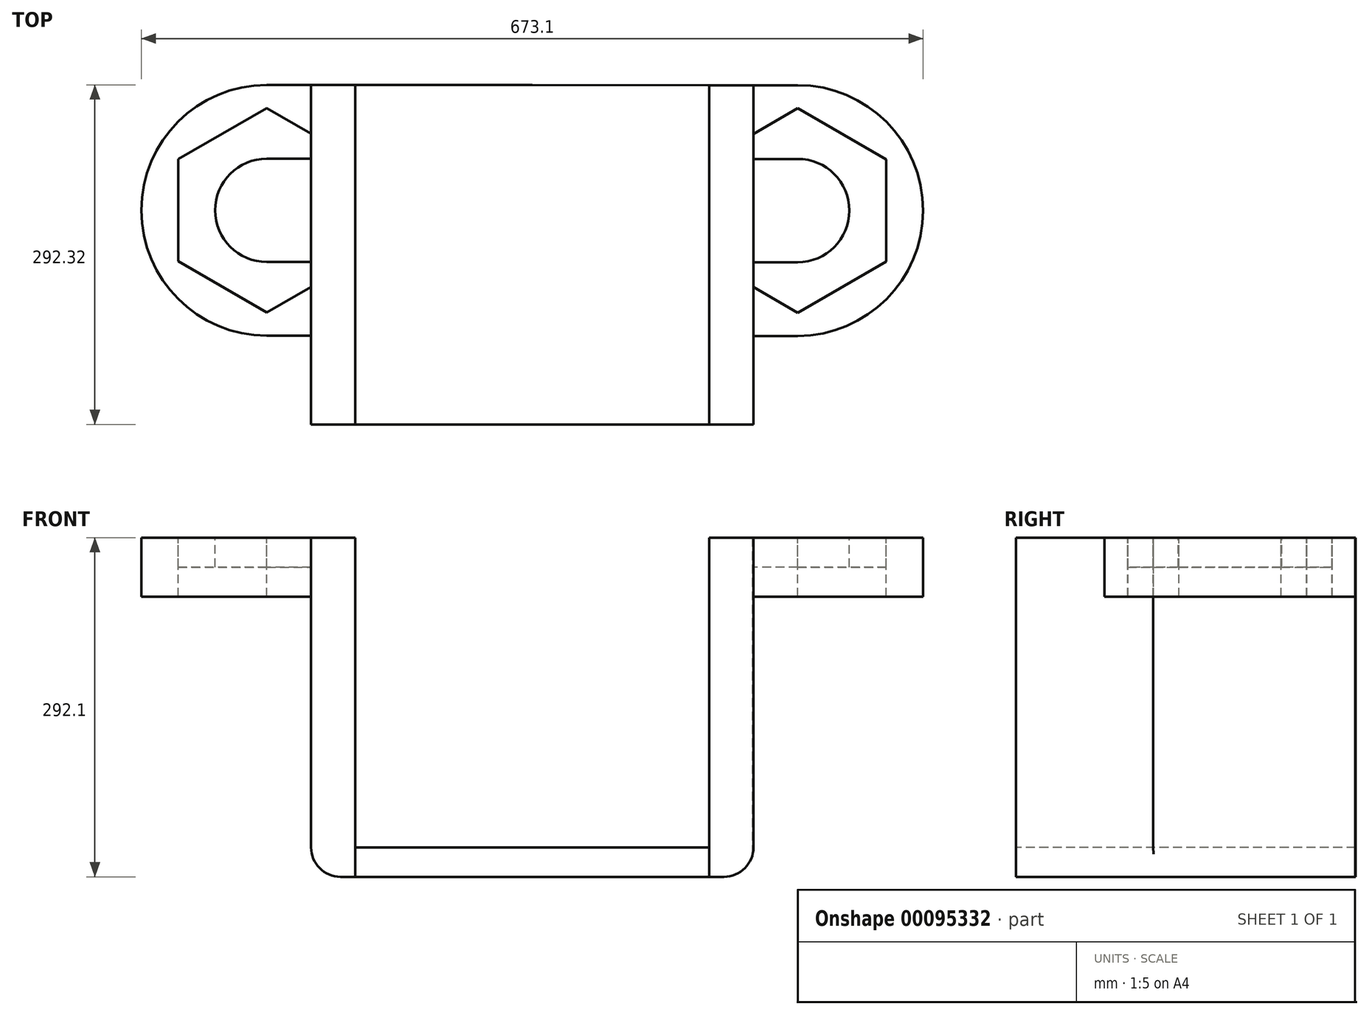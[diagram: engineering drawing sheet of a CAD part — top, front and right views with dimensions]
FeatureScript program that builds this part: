
annotation { "Feature Type Name" : "Feature", "Feature Type Description" : "" }
export const myFeature = defineFeature(function(context is Context, id is Id, definition is map)
    precondition{}
    {
        {
            var Q0;
            Q0=qCreatedBy(makeId("Top.planeOp"),FACE);
            var sketch = newSketch(context, id + "F0", { "sketchPlane" : qUnion([Q0])});
            skLineSegment(sketch, "E0.bottom", {"start": v(-146.94, 152.89) * mm, "end": v(157.86, 152.67) * mm});
            skLineSegment(sketch, "E0.left", {"start": v(-146.94, 152.89) * mm, "end": v(-146.94, 152.87) * mm});
            skPoint(sketch, "E0.middle", {"position": v(0, 0) * mm});
            skLineSegment(sketch, "E1.bottom", {"start": v(157.86, 152.67) * mm, "end": v(195.96, 152.67) * mm});
            skLineSegment(sketch, "E1.top", {"start": v(157.86, -139.43) * mm, "end": v(195.96, -139.43) * mm});
            skLineSegment(sketch, "E1.left", {"start": v(157.86, 152.67) * mm, "end": v(157.86, 45.47) * mm});
            skLineSegment(sketch, "E1.right", {"start": v(195.96, 152.67) * mm, "end": v(195.96, -139.43) * mm});
            skLineSegment(sketch, "E2.bottom", {"start": v(-146.94, 152.89) * mm, "end": v(-185.04, 152.89) * mm});
            skLineSegment(sketch, "E2.top", {"start": v(-146.94, -139.43) * mm, "end": v(-185.04, -139.43) * mm});
            skLineSegment(sketch, "E2.left", {"start": v(-146.94, 152.89) * mm, "end": v(-146.94, -139.43) * mm});
            skLineSegment(sketch, "E2.right", {"start": v(-185.04, 152.89) * mm, "end": v(-185.04, -139.43) * mm});
            skLineSegment(sketch, "E3", {"start": v(-185.04, 152.89) * mm, "end": v(-223.14, 152.89) * mm});
            skLineSegment(sketch, "E4", {"start": v(195.96, 152.67) * mm, "end": v(234.06, 152.67) * mm});
            skLineSegment(sketch, "E5", {"start": v(195.96, -63.23) * mm, "end": v(234.06, -63.23) * mm});
            skLineSegment(sketch, "E6", {"start": v(-223.14, -63.01) * mm, "end": v(-185.04, -63.01) * mm});
            skArc(sketch, "E7", {"start": v(234.06, 152.67) * mm, "mid": v(342.01, 44.72) * mm, "end": v(234.06, -63.23) * mm});
            skArc(sketch, "E8", {"start": v(-223.14, 152.89) * mm, "mid": v(-331.09, 44.94) * mm, "end": v(-223.14, -63.01) * mm});
            skLineSegment(sketch, "E9", {"start": v(-185.04, 152.89) * mm, "end": v(195.96, 152.67) * mm});
            skLineSegment(sketch, "E10", {"start": v(195.96, -139.43) * mm, "end": v(-185.04, -139.43) * mm});
            skLineSegment(sketch, "E11", {"start": v(-185.04, -139.43) * mm, "end": v(195.96, -139.43) * mm});
            skLineSegment(sketch, "E12", {"start": v(-232.75, -62.58) * mm, "end": v(-232.75, -63.01) * mm});
            skLineSegment(sketch, "E13", {"start": v(-185.04, 152.89) * mm, "end": v(-146.94, 152.89) * mm});
            skLineSegment(sketch, "E14", {"start": v(-185.04, -139.43) * mm, "end": v(-146.94, -139.43) * mm});
            skPoint(sketch, "E15.trimOffspring.end.orphan", {"position": v(-157.86, -152.67) * mm});
            skLineSegment(sketch, "E16.0", {"start": v(-146.93, 88.94) * mm, "end": v(-146.94, 0.94) * mm});
            skLineSegment(sketch, "E16.1", {"start": v(-185.06, -21.06) * mm, "end": v(-223.16, -43.04) * mm});
            skLineSegment(sketch, "E16.2", {"start": v(-223.16, -43.04) * mm, "end": v(-299.35, 0.96) * mm});
            skLineSegment(sketch, "E16.3", {"start": v(-299.35, 0.96) * mm, "end": v(-299.34, 88.95) * mm});
            skLineSegment(sketch, "E16.4", {"start": v(-299.34, 88.95) * mm, "end": v(-223.14, 132.92) * mm});
            skLineSegment(sketch, "E16.5", {"start": v(-223.14, 132.92) * mm, "end": v(-185.04, 110.93) * mm});
            skPoint(sketch, "E16.0.midPoint", {"position": v(-146.94, 44.94) * mm});
            skLineSegment(sketch, "E17.5", {"start": v(195.96, -21.28) * mm, "end": v(195.32, -20.9) * mm});
            skPoint(sketch, "E17.0.midPoint", {"position": v(157.86, 45.47) * mm});
            skLineSegment(sketch, "E18", {"start": v(195.96, 152.67) * mm, "end": v(195.96, -63.23) * mm});
            skLineSegment(sketch, "E19", {"start": v(-185.04, 152.89) * mm, "end": v(-185.04, -63.01) * mm});
            skLineSegment(sketch, "E20", {"start": v(-276.99, 138.5) * mm, "end": v(-276.99, 101.84) * mm});
            skLineSegment(sketch, "E21", {"start": v(-277, -11.95) * mm, "end": v(-277, -48.62) * mm});
            skPoint(sketch, "E22.trimOffspring.end.orphan", {"position": v(146.94, -152.89) * mm});
            skLineSegment(sketch, "E23", {"start": v(157.86, 152.67) * mm, "end": v(157.86, -139.43) * mm});
            skLineSegment(sketch, "E24.0", {"start": v(157.86, 0.73) * mm, "end": v(157.86, 88.71) * mm});
            skLineSegment(sketch, "E24.1", {"start": v(195.96, 110.71) * mm, "end": v(234.06, 132.7) * mm});
            skLineSegment(sketch, "E24.2", {"start": v(234.06, 132.7) * mm, "end": v(310.26, 88.71) * mm});
            skLineSegment(sketch, "E24.3", {"start": v(310.26, 88.71) * mm, "end": v(310.26, 0.73) * mm});
            skLineSegment(sketch, "E24.4", {"start": v(310.26, 0.73) * mm, "end": v(234.06, -43.27) * mm});
            skLineSegment(sketch, "E24.5", {"start": v(234.06, -43.27) * mm, "end": v(195.32, -20.9) * mm});
            skPoint(sketch, "E24.0.midPoint", {"position": v(157.86, 44.72) * mm});
            skLineSegment(sketch, "E25", {"start": v(288.01, 138.22) * mm, "end": v(288.01, 101.56) * mm});
            skLineSegment(sketch, "E26", {"start": v(288.01, -48.78) * mm, "end": v(288.01, -12.12) * mm});
            skLineSegment(sketch, "E27.trimOffspring", {"start": v(288.01, -12.12) * mm, "end": v(288.01, -48.78) * mm});
            skArc(sketch, "E28", {"start": v(-223.14, 89.39) * mm, "mid": v(-267.59, 44.94) * mm, "end": v(-223.14, 0.49) * mm});
            skArc(sketch, "E29", {"start": v(234.06, 89.17) * mm, "mid": v(278.51, 44.72) * mm, "end": v(234.06, 0.27) * mm});
            skLineSegment(sketch, "E30", {"start": v(234.06, 89.17) * mm, "end": v(195.96, 89.17) * mm});
            skLineSegment(sketch, "E31", {"start": v(234.06, 0.27) * mm, "end": v(195.96, 0.27) * mm});
            skLineSegment(sketch, "E32", {"start": v(-223.14, 0.49) * mm, "end": v(-185.04, 0.49) * mm});
            skLineSegment(sketch, "E33", {"start": v(-223.14, 89.39) * mm, "end": v(-185.04, 89.39) * mm});
            skLineSegment(sketch, "E34", {"start": v(-185.06, -21.06) * mm, "end": v(-185.04, -63.01) * mm});
            skLineSegment(sketch, "E35", {"start": v(-185.06, -21.06) * mm, "end": v(-185.04, 0.49) * mm});
            skLineSegment(sketch, "E36", {"start": v(-185.04, 0.49) * mm, "end": v(-223.14, 0.49) * mm});
            skSolve(sketch);
        }
        {
            var Q0;
            {var subQ4=sQuery(id+"F0.wireOp",EDGE,"E2.right");Q0=makeQuery(id+"F0.imprint","IMPRINT",FACE,{"disambiguationData":[TD([[makeQuery(id+"F0.imprint","IMPRINT",EDGE,{"derivedFrom":subQ4}),1.0]])]});}
            var Q1;
            {var subQ5=sQuery(id+"F0.wireOp",EDGE,"E1.right");Q1=makeQuery(id+"F0.imprint","IMPRINT",FACE,{"disambiguationData":[TD([[makeQuery(id+"F0.imprint","IMPRINT",EDGE,{"derivedFrom":subQ5}),-1.0]])]});}
            extrude(context, id + "F1", {"entities" : qUnion([Q0, Q1]), "oppositeDirection" : true, "depth" : 292.1 * mm});
        }
        {
            var Q0;
            {var subQ3=sQuery(id+"F0.wireOp",EDGE,"E2.left");var subQ7=makeQuery(id+"F0.imprint","IMPRINT",VERTEX,{"derivedFrom":subQ3});Q0=makeQuery(id+"F0.imprint","IMPRINT",FACE,{"disambiguationData":[TD([[makeQuery(id+"F0.imprint","IMPRINT",EDGE,{"disambiguationData":[TD([[subQ7,1.0]])],"derivedFrom":subQ3}),1.0]])]});}
            extrude(context, id + "F2", {"entities" : qUnion([Q0]), "oppositeDirection" : true, "depth" : 292.1 * mm});
        }
        {
            var Q0;
            {var subQ1=sQuery(id+"F0.wireOp",EDGE,"E16.3");Q0=makeQuery(id+"F0.imprint","IMPRINT",FACE,{"disambiguationData":[TD([[makeQuery(id+"F0.imprint","IMPRINT",EDGE,{"derivedFrom":subQ1}),1.0]])]});}
            var Q1;
            {var subQ3=sQuery(id+"F0.wireOp",EDGE,"E3");Q1=makeQuery(id+"F0.imprint","IMPRINT",FACE,{"disambiguationData":[TD([[makeQuery(id+"F0.imprint","IMPRINT",EDGE,{"derivedFrom":subQ3}),1.0]])]});}
            var Q2;
            {var subQ4=sQuery(id+"F0.wireOp",EDGE,"E6");Q2=makeQuery(id+"F0.imprint","IMPRINT",FACE,{"disambiguationData":[TD([[makeQuery(id+"F0.imprint","IMPRINT",EDGE,{"derivedFrom":subQ4}),1.0]])]});}
            var Q3;
            {var subQ8=sQuery(id+"F0.wireOp",EDGE,"E5");Q3=makeQuery(id+"F0.imprint","IMPRINT",FACE,{"disambiguationData":[TD([[makeQuery(id+"F0.imprint","IMPRINT",EDGE,{"derivedFrom":subQ8}),1.0]])]});}
            var Q4;
            {var subQ1=sQuery(id+"F0.wireOp",EDGE,"E24.3");Q4=makeQuery(id+"F0.imprint","IMPRINT",FACE,{"disambiguationData":[TD([[makeQuery(id+"F0.imprint","IMPRINT",EDGE,{"derivedFrom":subQ1}),1.0]])]});}
            var Q5;
            {var subQ2=sQuery(id+"F0.wireOp",EDGE,"E4");Q5=makeQuery(id+"F0.imprint","IMPRINT",FACE,{"disambiguationData":[TD([[makeQuery(id+"F0.imprint","IMPRINT",EDGE,{"derivedFrom":subQ2}),-1.0]])]});}
            extrude(context, id + "F3", {"entities" : qUnion([Q0, Q1, Q2, Q3, Q4, Q5]), "oppositeDirection" : true, "depth" : 50.8 * mm});
        }
        {
            var Q0;
            {var subQ8=sQuery(id+"F0.wireOp",EDGE,"E24.1");Q0=makeQuery(id+"F0.imprint","IMPRINT",FACE,{"disambiguationData":[TD([[makeQuery(id+"F0.imprint","IMPRINT",EDGE,{"derivedFrom":subQ8}),-1.0]])]});}
            var Q1;
            {var subQ5=sQuery(id+"F0.wireOp",EDGE,"E16.3");Q1=makeQuery(id+"F0.imprint","IMPRINT",FACE,{"disambiguationData":[TD([[makeQuery(id+"F0.imprint","IMPRINT",EDGE,{"derivedFrom":subQ5}),-1.0]])]});}
            extrude(context, id + "F4", {"entities" : qUnion([Q0, Q1]), "oppositeDirection" : true, "depth" : 25.4 * mm});
        }
        {
            var Q0;
            {var subQ3=sQuery(id+"F0.wireOp",EDGE,"E2.left");var subQ7=makeQuery(id+"F0.imprint","IMPRINT",VERTEX,{"derivedFrom":subQ3});Q0=makeQuery(id+"F0.imprint","IMPRINT",FACE,{"disambiguationData":[TD([[makeQuery(id+"F0.imprint","IMPRINT",EDGE,{"disambiguationData":[TD([[subQ7,1.0]])],"derivedFrom":subQ3}),1.0]])]});}
            extrude(context, id + "F5", {"entities" : qUnion([Q0]), "operationType" : NewBodyOperationType.REMOVE, "oppositeDirection" : true, "depth" : 266.7 * mm});
        }
        {
            var Q0;
            Q0=makeQuery(id+"F1.opExtrude","CAP_EDGE",EDGE,{"disambiguationData":[OSD([sQuery(id+"F0.wireOp",EDGE,"E2.right"),sQuery(id+"F0.wireOp",EDGE,"E19")])],"isStart":false});
            fillet(context, id + "F6", {"entities" : qUnion([Q0]), "radius" : 25.4 * mm, "tangentPropagation" : true, "allowEdgeOverflow" : false});
        }
        {
            var Q0;
            Q0=makeQuery(id+"F1.opExtrude","CAP_EDGE",EDGE,{"disambiguationData":[OSD([sQuery(id+"F0.wireOp",EDGE,"E1.right"),sQuery(id+"F0.wireOp",EDGE,"E18")])],"isStart":false});
            var Q1;
            Q1=makeQuery(id+"F1.opExtrude","CAP_EDGE",EDGE,{"disambiguationData":[OSD([sQuery(id+"F0.wireOp",EDGE,"E18")])],"isStart":false});
            fillet(context, id + "F7", {"entities" : qUnion([Q0, Q1]), "radius" : 25.4 * mm, "tangentPropagation" : true, "allowEdgeOverflow" : false});
        }
    });
